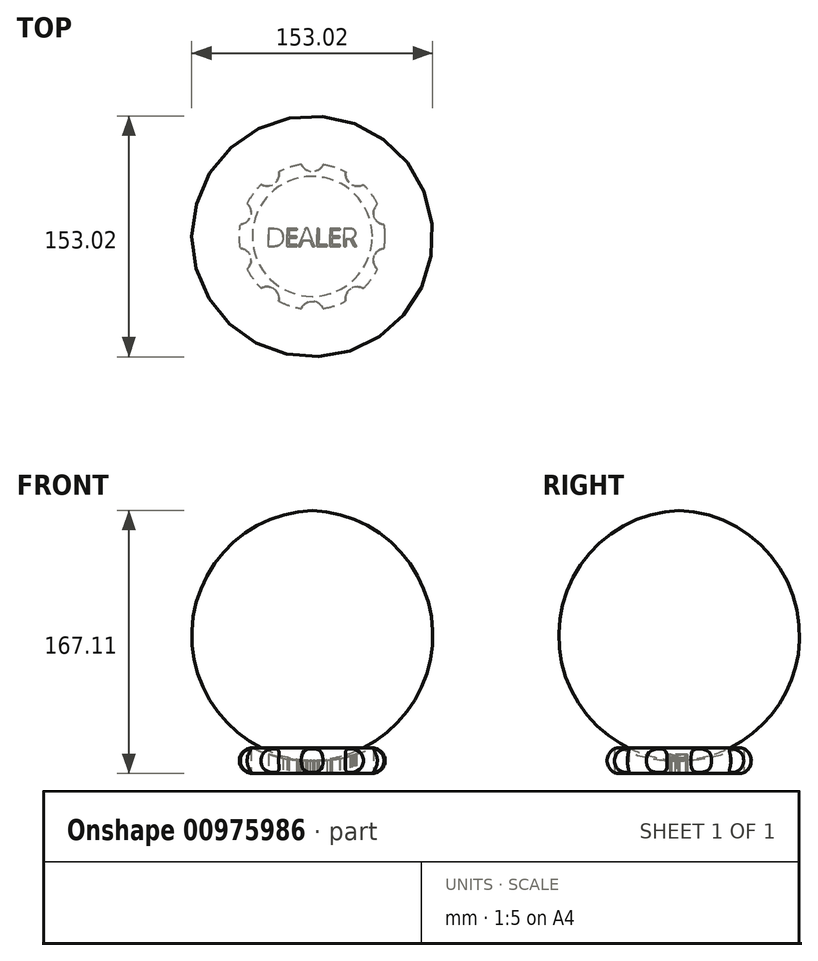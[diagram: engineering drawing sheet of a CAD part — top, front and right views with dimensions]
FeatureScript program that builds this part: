
annotation { "Feature Type Name" : "Feature", "Feature Type Description" : "" }
export const myFeature = defineFeature(function(context is Context, id is Id, definition is map)
    precondition{}
    {
        {
            var Q0;
            Q0=qCreatedBy(makeId("Front.planeOp"),FACE);
            var sketch = newSketch(context, id + "F0", { "sketchPlane" : qUnion([Q0])});
            skLineSegment(sketch, "E0", {"start": v(0, 0) * mm, "end": v(38.1, 0) * mm});
            skPoint(sketch, "E1.start.orphan", {"position": v(0, 8.2) * mm});
            skArc(sketch, "E2", {"start": v(38.1, 0) * mm, "mid": v(46.26, 8.16) * mm, "end": v(38.1, 16.32) * mm});
            skArc(sketch, "E3", {"start": v(0, 8.2) * mm, "mid": v(19.55, 9.9) * mm, "end": v(38.1, 16.32) * mm});
            skLineSegment(sketch, "E4", {"start": v(0, 8.2) * mm, "end": v(0, 0) * mm});
            skSolve(sketch);
        }
        {
            var Q0;
            Q0=makeQuery(id+"F0.imprint","IMPRINT",FACE,{"disambiguationData":[TD([[makeQuery(id+"F0.imprint","IMPRINT",EDGE,{"derivedFrom":sQuery(id+"F0.wireOp",EDGE,"E0")}),1.0]])]});
            var Q1;
            Q1=sQuery(id+"F0.wireOp",EDGE,"E4");
            revolve(context, id + "F1", {"surfaceOperationType" : NewSurfaceOperationType.NEW, "entities" : qUnion([Q0]), "axis" : qUnion([Q1]), "revolveType" : RevolveType.FULL});
        }
        {
            var Q0;
            Q0=qCreatedBy(makeId("Top.planeOp"),FACE);
            var sketch = newSketch(context, id + "F2", { "sketchPlane" : qUnion([Q0])});
            skText(sketch, "E5", { "text": "DEALER", "fontName": "OpenSans-Regular.ttf"});
            const initialGuessF2  = {"E5": [-0.0292, -0.00626, 1, 0, 0.0115]};
            skSetInitialGuess(sketch, initialGuessF2);
            skSolve(sketch);
        }
        {
            var Q0;
            Q0=makeQuery(id+"F2.imprint","IMPRINT",FACE,{"disambiguationData":[TD([[makeQuery(id+"F2.imprint","IMPRINT",EDGE,{"derivedFrom":sQuery(id+"F2.wireOp",EDGE,"E5.sketch_text.stroke-14")}),-1.0]])]});
            var Q1;
            Q1=makeQuery(id+"F2.imprint","IMPRINT",FACE,{"disambiguationData":[TD([[makeQuery(id+"F2.imprint","IMPRINT",EDGE,{"derivedFrom":sQuery(id+"F2.wireOp",EDGE,"E5.sketch_text.stroke-34")}),1.0]])]});
            var Q2;
            Q2=makeQuery(id+"F2.imprint","IMPRINT",FACE,{"disambiguationData":[TD([[makeQuery(id+"F2.imprint","IMPRINT",EDGE,{"derivedFrom":sQuery(id+"F2.wireOp",EDGE,"E5.sketch_text.stroke-26")}),-1.0]])]});
            var Q3;
            Q3=makeQuery(id+"F2.imprint","IMPRINT",FACE,{"disambiguationData":[TD([[makeQuery(id+"F2.imprint","IMPRINT",EDGE,{"derivedFrom":sQuery(id+"F2.wireOp",EDGE,"E5.sketch_text.stroke-0")}),-1.0]])]});
            var Q4;
            Q4=makeQuery(id+"F2.imprint","IMPRINT",FACE,{"disambiguationData":[TD([[makeQuery(id+"F2.imprint","IMPRINT",EDGE,{"derivedFrom":sQuery(id+"F2.wireOp",EDGE,"E5.sketch_text.stroke-39")}),-1.0]])]});
            var Q5;
            Q5=makeQuery(id+"F2.imprint","IMPRINT",FACE,{"disambiguationData":[TD([[makeQuery(id+"F2.imprint","IMPRINT",EDGE,{"derivedFrom":sQuery(id+"F2.wireOp",EDGE,"E5.sketch_text.stroke-45")}),-1.0]])]});
            var Q6;
            Q6=makeQuery(id+"F2.imprint","IMPRINT",FACE,{"disambiguationData":[TD([[makeQuery(id+"F2.imprint","IMPRINT",EDGE,{"derivedFrom":sQuery(id+"F2.wireOp",EDGE,"E5.sketch_text.stroke-68")}),1.0]])]});
            var Q7;
            Q7=makeQuery(id+"F2.imprint","IMPRINT",FACE,{"disambiguationData":[TD([[makeQuery(id+"F2.imprint","IMPRINT",EDGE,{"derivedFrom":sQuery(id+"F2.wireOp",EDGE,"E5.sketch_text.stroke-57")}),-1.0]])]});
            var Q8;
            Q8=makeQuery(id+"F2.imprint","IMPRINT",FACE,{"disambiguationData":[TD([[makeQuery(id+"F2.imprint","IMPRINT",EDGE,{"derivedFrom":sQuery(id+"F2.wireOp",EDGE,"E5.sketch_text.stroke-7")}),1.0]])]});
            extrude(context, id + "F3", {"entities" : qUnion([Q0, Q1, Q2, Q3, Q4, Q5, Q6, Q7, Q8]), "operationType" : NewBodyOperationType.REMOVE, "depth" : 57.44 * mm, "offsetDistance" : 25.4 * mm});
        }
        {
            var Q0;
            Q0=qCreatedBy(makeId("Top.planeOp"),FACE);
            var sketch = newSketch(context, id + "F4", { "sketchPlane" : qUnion([Q0])});
            skCircle(sketch, "E6", {"center": v(0.08, 48.8) * mm, "radius": 7.57 * mm});
            skCircle(sketch, "E7.1.0", {"center": v(-28.63, 39.53) * mm, "radius": 7.57 * mm});
            skCircle(sketch, "E7.2.0", {"center": v(-46.4, 15.15) * mm, "radius": 7.57 * mm});
            skCircle(sketch, "E7.3.0", {"center": v(-46.44, -15.01) * mm, "radius": 7.57 * mm});
            skCircle(sketch, "E7.4.0", {"center": v(-28.75, -39.44) * mm, "radius": 7.57 * mm});
            skCircle(sketch, "E7.5.0", {"center": v(-0.08, -48.8) * mm, "radius": 7.57 * mm});
            skCircle(sketch, "E7.6.0", {"center": v(28.63, -39.53) * mm, "radius": 7.57 * mm});
            skCircle(sketch, "E7.7.0", {"center": v(46.4, -15.15) * mm, "radius": 7.57 * mm});
            skCircle(sketch, "E7.8.0", {"center": v(46.44, 15.01) * mm, "radius": 7.57 * mm});
            skCircle(sketch, "E7.9.0", {"center": v(28.75, 39.44) * mm, "radius": 7.57 * mm});
            skPoint(sketch, "E7.center", {"position": v(0, 0) * mm});
            skSolve(sketch);
        }
        {
            var Q0;
            Q0=makeQuery(id+"F4.imprint","IMPRINT",FACE,{"disambiguationData":[TD([[makeQuery(id+"F4.imprint","IMPRINT",EDGE,{"derivedFrom":sQuery(id+"F4.wireOp",EDGE,"E6")}),1.0]])]});
            var Q1;
            Q1=makeQuery(id+"F4.imprint","IMPRINT",FACE,{"disambiguationData":[TD([[makeQuery(id+"F4.imprint","IMPRINT",EDGE,{"derivedFrom":sQuery(id+"F4.wireOp",EDGE,"E7.9.0")}),1.0]])]});
            var Q2;
            Q2=makeQuery(id+"F4.imprint","IMPRINT",FACE,{"disambiguationData":[TD([[makeQuery(id+"F4.imprint","IMPRINT",EDGE,{"derivedFrom":sQuery(id+"F4.wireOp",EDGE,"E7.8.0")}),1.0]])]});
            var Q3;
            Q3=makeQuery(id+"F4.imprint","IMPRINT",FACE,{"disambiguationData":[TD([[makeQuery(id+"F4.imprint","IMPRINT",EDGE,{"derivedFrom":sQuery(id+"F4.wireOp",EDGE,"E7.7.0")}),1.0]])]});
            var Q4;
            Q4=makeQuery(id+"F4.imprint","IMPRINT",FACE,{"disambiguationData":[TD([[makeQuery(id+"F4.imprint","IMPRINT",EDGE,{"derivedFrom":sQuery(id+"F4.wireOp",EDGE,"E7.6.0")}),1.0]])]});
            var Q5;
            Q5=makeQuery(id+"F4.imprint","IMPRINT",FACE,{"disambiguationData":[TD([[makeQuery(id+"F4.imprint","IMPRINT",EDGE,{"derivedFrom":sQuery(id+"F4.wireOp",EDGE,"E7.5.0")}),1.0]])]});
            var Q6;
            Q6=makeQuery(id+"F4.imprint","IMPRINT",FACE,{"disambiguationData":[TD([[makeQuery(id+"F4.imprint","IMPRINT",EDGE,{"derivedFrom":sQuery(id+"F4.wireOp",EDGE,"E7.4.0")}),1.0]])]});
            var Q7;
            Q7=makeQuery(id+"F4.imprint","IMPRINT",FACE,{"disambiguationData":[TD([[makeQuery(id+"F4.imprint","IMPRINT",EDGE,{"derivedFrom":sQuery(id+"F4.wireOp",EDGE,"E7.1.0")}),1.0]])]});
            var Q8;
            Q8=makeQuery(id+"F4.imprint","IMPRINT",FACE,{"disambiguationData":[TD([[makeQuery(id+"F4.imprint","IMPRINT",EDGE,{"derivedFrom":sQuery(id+"F4.wireOp",EDGE,"E7.2.0")}),1.0]])]});
            var Q9;
            Q9=makeQuery(id+"F4.imprint","IMPRINT",FACE,{"disambiguationData":[TD([[makeQuery(id+"F4.imprint","IMPRINT",EDGE,{"derivedFrom":sQuery(id+"F4.wireOp",EDGE,"E7.3.0")}),1.0]])]});
            extrude(context, id + "F5", {"entities" : qUnion([Q0, Q1, Q2, Q3, Q4, Q5, Q6, Q7, Q8, Q9]), "operationType" : NewBodyOperationType.REMOVE, "depth" : 76 * mm, "offsetDistance" : 25.4 * mm});
        }
    });
